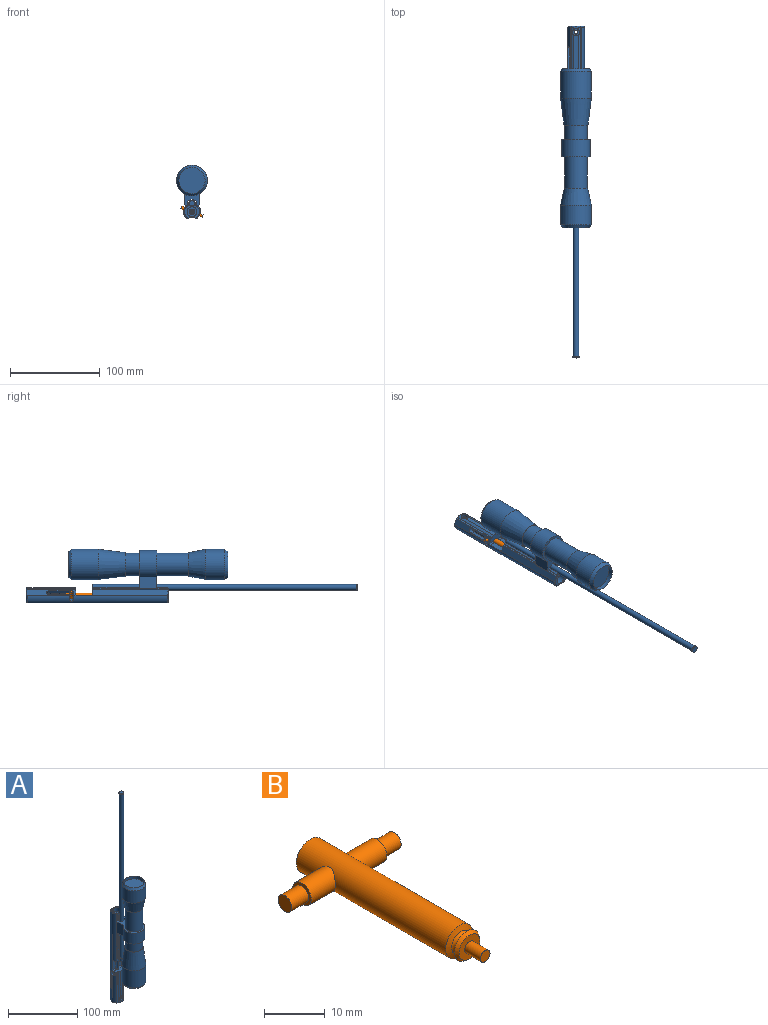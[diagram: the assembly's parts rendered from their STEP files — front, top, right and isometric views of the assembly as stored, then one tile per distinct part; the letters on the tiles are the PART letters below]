
ASSEMBLY  parts=2 mates=1
PART A: 113 faces, bbox 34.4x60.6x370.7 mm
  f0: plane 52.39x2.02mm, normal (0,-1,0), area 105.6mm2, adj f2,f10,f13,f97
  f1: plane 52.39x2.02mm, normal (0,-1,0), area 105.6mm2, adj f3,f10,f72,f97
  f2: plane 52.39x1.06mm, normal (-0.83,0.56,0), area 66.1mm2, adj f0,f4,f8,f10,f80,f81,f82,f97
  f3: plane 52.39x1.06mm, normal (0.83,0.56,0), area 66.5mm2, adj f1,f9,f10,f97
  f4: cylinder r=9.53mm len=78.04mm, axis (0,0,-1), area 188.5mm2, adj f2,f6,f40,f73,f82,f83,f89
  f5: cylinder r=2.92mm len=294.64mm, axis (0,0,-1), area 5401mm2, adj f10,f77,f78,f79,f80,f81,f82,f83
  f6: cone r=8.02mm half-angle=62.4deg, axis (0,0,-1), area 23.8mm2, adj f4,f13,f14,f37,f39,f40,f43,f70
  f7: cone r=8.02mm half-angle=62.4deg, axis (0,0,-1), area 23.8mm2, adj f9,f25,f37,f41,f42,f43,f72,f73
  f8: cylinder r=9.53mm len=5.02mm, axis (0,0,-1), area 11mm2, adj f2,f10,f73,f79,f80
  f9: cylinder r=9.53mm len=83.46mm, axis (0,0,-1), area 202.9mm2, adj f3,f7,f10,f41,f73,f86
  f10: plane 18.24x11.11mm, normal (0,0,-1), area 90.8mm2, adj f0,f1,f2,f3,f5,f8,f9,f13
  f11: cylinder r=2.38mm len=7.39mm, axis (-0.92,0.39,0.01), area 25.4mm2, adj f17,f19,f21,f70
  f12: cylinder r=9.53mm len=56.01mm, axis (0,0,-1), area 390.7mm2, adj f15,f19,f20,f23,f30,f48,f50,f69
  f13: cylinder r=9.53mm len=85.04mm, axis (0,0,-1), area 639.6mm2, adj f0,f6,f10,f39,f47,f70,f90
  f14: cylinder r=9.53mm len=156.93mm, axis (0,0,-1), area 230.7mm2, adj f6,f15,f43,f70
  f15: cone r=7.93mm half-angle=54.5deg, axis (0,0,1), area 75.5mm2, adj f12,f14,f25,f30,f31,f32,f33,f34
  f16: cylinder r=2.38mm len=7.94mm, axis (-0.92,0.39,0.01), area 45mm2, adj f17,f18,f21,f54,f70
  f17: plane 25.58x6.44mm, normal (-0.39,-0.92,0), area 160.4mm2, adj f11,f16,f21,f22,f54,f70
  f18: plane 23x6.08mm, normal (0.39,0.92,0), area 151.1mm2, adj f16,f20,f21,f23,f70
  f19: plane 6.74x6.59mm, normal (0,0,-1), area 28.6mm2, adj f11,f12,f21,f69,f70
  f20: plane 6.08x4.47mm, normal (0,0,1), area 13.9mm2, adj f12,f18,f23,f70
  f21: cylinder r=3.17mm len=76.2mm, axis (0,0,-1), area 867mm2, adj f10,f11,f16,f17,f18,f19,f22,f23
  f22: cylinder r=1.59mm len=3.71mm, axis (0,-1,0), area 16.9mm2, adj f17,f21,f43,f54,f56
  f23: cylinder r=2.38mm len=7.84mm, axis (0.92,0.39,0.01), area 51.8mm2, adj f12,f18,f20,f21,f69
  f24: cylinder r=2.38mm len=8.1mm, axis (0.92,0.39,0.01), area 54.2mm2, adj f21,f25,f63,f65,f67
  f25: cylinder r=9.53mm len=156.93mm, axis (0,0,-1), area 1404.6mm2, adj f7,f15,f24,f43,f51,f65,f66,f67
  f26: cylinder r=2.38mm len=6.94mm, axis (0.92,-0.39,-0.01), area 22.2mm2, adj f21,f62,f68,f71
  f27: plane 45.25x4.77mm, normal (0,-1,0), area 213.2mm2, adj f32,f34,f48,f60
  f28: cylinder r=1.98mm len=3.97mm, axis (0,1,0), area 40mm2, adj f21,f61
  f29: cylinder r=1.59mm len=3.18mm, axis (0,-1,0), area 22.8mm2, adj f43,f58
  f30: plane 55.48x2.16mm, normal (0,-1,0), area 110.6mm2, adj f12,f15,f31,f48
  f31: plane 55.33x1.06mm, normal (-0.83,0.56,0), area 69.7mm2, adj f15,f30,f32,f48
  f32: cylinder r=9.53mm len=54.42mm, axis (0,0,-1), area 167.3mm2, adj f15,f27,f31,f33,f48,f60
  f33: plane 4.77x3.05mm, normal (0,-1,0), area 11.6mm2, adj f15,f32,f34,f60
  f34: cylinder r=9.53mm len=54.42mm, axis (0,0,-1), area 167.3mm2, adj f15,f27,f33,f35,f48,f60
  f35: plane 55.33x1.06mm, normal (0.83,0.56,0), area 69.7mm2, adj f15,f34,f36,f48
  f36: plane 55.48x2.16mm, normal (0,-1,0), area 110.6mm2, adj f15,f35,f48,f71
  f37: plane 16.43x14.91mm, normal (0,0,1), area 98mm2, adj f6,f7,f43,f44,f73
  f38: plane 15.86x14.93mm, normal (0,0,-1), area 158mm2, adj f15,f21,f43
  f39: plane 12.82x2.16mm, normal (0,-1,0), area 24.9mm2, adj f6,f13,f40,f98
  f40: plane 12.68x1.06mm, normal (-0.83,0.56,0), area 15.7mm2, adj f4,f6,f39,f98
  f41: plane 12.68x1.06mm, normal (0.83,0.56,0), area 15.7mm2, adj f7,f9,f42,f98
  f42: plane 12.82x2.16mm, normal (0,-1,0), area 24.9mm2, adj f7,f41,f72,f98
  f43: cylinder r=11.11mm len=158.75mm, axis (0,0,-1), area 1668.7mm2, adj f6,f7,f14,f15,f22,f25,f29,f37
  f44: cylinder r=5.56mm len=82.55mm, axis (0,0,1), area 2848.8mm2, adj f37,f45,f53
  f45: plane 11.11x11.11mm, normal (0,0,1), area 65.3mm2, adj f21,f44
  f46: cylinder r=1.59mm len=6.78mm, axis (1,0,0), area 15.5mm2, adj f10,f21,f51,f72
  f47: cylinder r=1.59mm len=6.78mm, axis (1,0,0), area 15.9mm2, adj f10,f13,f21,f52
  f48: plane 18.24x7.63mm, normal (0,0,1), area 99.7mm2, adj f12,f21,f27,f30,f31,f32,f34,f35
  f49: cylinder r=1.59mm len=6.78mm, axis (1,0,0), area 15.5mm2, adj f21,f48,f51,f71
  f50: cylinder r=1.59mm len=6.78mm, axis (1,0,0), area 15.9mm2, adj f12,f21,f48,f52
  f51: plane 15.88x6.35mm, normal (0,-1,0), area 100.8mm2, adj f21,f25,f46,f49
  f52: plane 15.88x6.35mm, normal (0,-1,0), area 100.8mm2, adj f21,f47,f50,f70
  f53: cylinder r=3.17mm len=6.35mm, axis (0,-1,0), area 30.1mm2, adj f43,f44
  f54: plane 27.09x3.82mm, normal (1,0,0), area 91.2mm2, adj f16,f17,f21,f22,f43,f55
  f55: cylinder r=1.59mm len=3.71mm, axis (0,-1,0), area 17.4mm2, adj f21,f43,f54,f56
  f56: plane 26.99x3.71mm, normal (-1,0,0), area 100.2mm2, adj f21,f22,f43,f55
  f57: cylinder r=1.98mm len=4.05mm, axis (0,-1,0), area 44.9mm2, adj f21,f43
  f58: plane 4.76x4.76mm, normal (0,-1,0), area 9.9mm2, adj f29,f59
  f59: cylinder r=2.38mm len=4.76mm, axis (0,-1,0), area 20.9mm2, adj f21,f58
  f60: cylinder r=3.97mm len=7.94mm, axis (0,-1,0), area 74.1mm2, adj f27,f32,f33,f34,f61
  f61: plane 7.94x7.94mm, normal (0,-1,0), area 37.1mm2, adj f28,f60
  f62: plane 25.44x6.1mm, normal (0.39,0.92,0), area 166.8mm2, adj f21,f26,f64,f71
  f63: plane 23.1x6.27mm, normal (-0.39,-0.92,0), area 156.1mm2, adj f21,f24,f64,f65,f66,f71
  f64: cylinder r=2.38mm len=8.06mm, axis (0.92,-0.39,-0.01), area 45.6mm2, adj f21,f62,f63,f71
  f65: plane 5.57x2.31mm, normal (0.38,-0.92,0), area 0.3mm2, adj f24,f25,f63,f66
  f66: plane 6.29x4.78mm, normal (0,0,1), area 15.3mm2, adj f25,f63,f65,f71
  f67: plane 6.72x6.59mm, normal (0,0,-1), area 28.4mm2, adj f21,f24,f25,f68,f71
  f68: plane 5.16x2.14mm, normal (0.38,0.92,0), area 0.2mm2, adj f21,f26,f67,f71
  f69: plane 5.87x2.44mm, normal (-0.38,0.92,0), area 0.2mm2, adj f12,f19,f21,f23
  f70: plane 157.9x6.89mm, normal (-0.92,0.39,0), area 1027.4mm2, adj f6,f11,f12,f13,f14,f15,f16,f17
  f71: plane 56.58x6.89mm, normal (0.92,-0.39,0), area 263mm2, adj f15,f25,f26,f36,f48,f49,f62,f63
  f72: plane 85.44x6.86mm, normal (0.92,-0.39,0), area 624.5mm2, adj f1,f7,f10,f25,f42,f46,f96
  f73: cylinder r=3.17mm len=294.64mm, axis (0,0,-1), area 5124.4mm2, adj f4,f6,f7,f8,f9,f10,f37,f74
  f74: plane 7.34x7.34mm, normal (0,0,-1), area 10.6mm2, adj f73,f76
  f75: plane 7.34x7.34mm, normal (0,0,1), area 42.3mm2, adj f76
  f76: cylinder r=3.67mm len=7.34mm, axis (0,0,-1), area 29.3mm2, adj f74,f75
  f77: plane 5.84x5.84mm, normal (0,0,-1), area 26.8mm2, adj f5
  f78: plane 1.47x1.29mm, normal (0,0,1), area 0.4mm2, adj f5,f73,f79,f85
  f79: cylinder r=1.27mm len=2.51mm, axis (1,0,0), area 2.3mm2, adj f5,f8,f73,f78,f80
  f80: plane 3.86x1.29mm, normal (0,0,1), area 3.6mm2, adj f2,f5,f8,f79,f81
  f81: plane 3.24x0.39mm, normal (0,-1,0), area 1.3mm2, adj f2,f5,f80,f82
  f82: plane 3.86x1.29mm, normal (0,0,-1), area 3.6mm2, adj f2,f4,f5,f81,f83
  f83: cylinder r=1.27mm len=2.51mm, axis (1,0,0), area 2.3mm2, adj f4,f5,f73,f82,f84
  f84: plane 1.47x1.29mm, normal (0,0,-1), area 0.4mm2, adj f5,f73,f83,f85
  f85: plane 0.46x0.39mm, normal (0,1,0), area 0.2mm2, adj f5,f73,f78,f84
  f86: plane 19.05x3.57mm, normal (-1,0,0), area 67.9mm2, adj f9,f87,f97,f98
  f87: plane 19.05x5.3mm, normal (-0.44,0.9,0), area 112.6mm2, adj f86,f88,f97,f98
  f88: plane 19.05x5.3mm, normal (0.44,0.9,0), area 112.6mm2, adj f87,f89,f97,f98
  f89: plane 19.05x3.57mm, normal (1,0,0), area 67.9mm2, adj f4,f88,f97,f98
  f90: plane 19.05x0.68mm, normal (0,1,0), area 13mm2, adj f13,f91,f97,f98
  f91: plane 19.05x1.06mm, normal (-0.79,0.61,0), area 25.3mm2, adj f90,f92,f97,f98
  f92: plane 19.05x13.54mm, normal (-1,0,0), area 258mm2, adj f91,f93,f97,f98
  f93: cylinder r=15.74mm len=31.48mm, axis (0,0,1), area 1559.7mm2, adj f92,f94,f97,f98
  f94: plane 19.05x13.54mm, normal (1,0,0), area 258mm2, adj f93,f95,f97,f98
  f95: plane 19.05x1.06mm, normal (0.79,0.61,0), area 25.3mm2, adj f94,f96,f97,f98
  f96: plane 19.05x0.68mm, normal (0,1,0), area 13mm2, adj f72,f95,f97,f98
  f97: plane 43.83x31.48mm, normal (0,0,-1), area 420.4mm2, adj f0,f1,f2,f3,f86,f87,f88,f89
  f98: plane 43.83x31.48mm, normal (0,0,1), area 420.4mm2, adj f39,f40,f41,f42,f86,f87,f88,f89
  f99: cylinder r=12.7mm len=34.93mm, axis (0,0,1), area 2786.9mm2, adj f98,f105
  f100: cylinder r=12.7mm len=25.4mm, axis (0,0,1), area 1266.8mm2, adj f97,f102
  f101: cylinder r=17.14mm len=34.29mm, axis (0,0,1), area 3228.7mm2, adj f103,f106
  f102: plane 26.67x26.67mm, normal (0,0,1), area 51.9mm2, adj f100,f103
  f103: cone r=17.14mm half-angle=7.1deg, axis (0,0,-1), area 2941.3mm2, adj f101,f102
  f104: cylinder r=17.14mm len=34.29mm, axis (0,0,-1), area 2325.8mm2, adj f109,f110
  f105: plane 26.16x26.16mm, normal (0,0,-1), area 30.9mm2, adj f99,f110
  f106: cone r=14.86mm half-angle=36.9deg, axis (0,0,1), area 383.1mm2, adj f101,f107
  f107: cylinder r=14.86mm len=29.72mm, axis (0,0,-1), area 237.1mm2, adj f106,f108
  f108: plane 29.72x29.72mm, normal (0,0,-1), area 693.6mm2, adj f107
  f109: cone r=14.61mm half-angle=33.7deg, axis (0,0,-1), area 456.7mm2, adj f104,f111
  f110: cone r=17.14mm half-angle=12deg, axis (0,0,1), area 1849.7mm2, adj f104,f105
  f111: cylinder r=14.61mm len=29.21mm, axis (0,0,1), area 466.2mm2, adj f109,f112
  f112: plane 29.21x29.21mm, normal (0,0,1), area 670.1mm2, adj f111
PART B: 17 faces, bbox 25.4x40.6x6.4 mm
  f0: cylinder r=3.17mm len=34.65mm, axis (0,1,0), area 659.8mm2, adj f1,f2,f10,f11
  f1: plane 6.35x6.35mm, normal (0,1,0), area 31.7mm2, adj f0
  f2: cone r=3.69mm half-angle=70deg, axis (0,1,0), area 18.3mm2, adj f0,f3
  f3: torus R=2.38mm, axis (0,1,0), area 15.5mm2, adj f2,f4
  f4: cone r=2.15mm half-angle=65deg, axis (0,-1,0), area 12.8mm2, adj f3,f5
  f5: cone r=2.88mm half-angle=36.9deg, axis (0,1,0), area 13mm2, adj f4,f6
  f6: plane 4.82x4.82mm, normal (0,-1,0), area 14.3mm2, adj f5,f7
  f7: cylinder r=1.12mm len=3.63mm, axis (0,1,0), area 25.6mm2, adj f6,f8
  f8: plane 2.24x2.24mm, normal (0,-1,0), area 4mm2, adj f7
  f9: plane 4.32x4.32mm, normal (-1,0,0), area 6.7mm2, adj f10,f15
  f10: cylinder r=2.16mm len=6.44mm, axis (-1,0,0), area 81.4mm2, adj f0,f9
  f11: cylinder r=2.16mm len=6.44mm, axis (-1,0,0), area 81.4mm2, adj f0,f12
  f12: plane 4.32x4.32mm, normal (1,0,0), area 6.7mm2, adj f11,f14
  f13: plane 3.18x3.18mm, normal (1,0,0), area 7.9mm2, adj f14
  f14: cylinder r=1.59mm len=3.93mm, axis (-1,0,0), area 39.2mm2, adj f12,f13
  f15: cylinder r=1.59mm len=3.93mm, axis (-1,0,0), area 39.2mm2, adj f9,f16
  f16: plane 3.18x3.18mm, normal (-1,0,0), area 7.9mm2, adj f15
PLACE A rot(axis=(0,-0.71,0.71),180deg) t=(0,0,0)mm fixed
PLACE B rot(axis=(0,-1,0),158deg) t=(0,-43.94,0)mm
MATE cylindrical B.f0 <-> A.f6  axis (0,1,0) through (0,-43.94,0)mm
